# Revit family: Graypants_Chrona_Sconce10_R21_0925
name_source: partatom
category: Lighting Fixtures
units: mm (PartAtom-declared; Revit-internal decimal feet)

## family parameters
Cut with Voids When Loaded = No
Host = Face
Light Source = Yes
Part Type = Normal
Room Calculation Point = No
Round Connector Dimension = Use Diameter
Shared = No

## types (1)
- Graypants_Chrona_Sconce10 (diameter 10")
    Color Filter = 16777215
    Default Elevation = 4' - 0"
    Dimming Lamp Color Temperature Shift = <None>
    Graypants_Apparent_Load = Sconce10 - 12W
    Graypants_Cord_Material_Finish = _Graypants_Black_Finish
    Graypants_Description = Mimicking the phosphorescent envelope found around stars, Chrona lights create a luminous glow by combining spun brass and diffused acrylic. 
With a variety of configurations in both horizontal and vertical orientations, Dish pendants can be clustered together to make stunning 
constellations or individually hung to accentuate any space.
    Graypants_Dimming = 0-10v
    Graypants_Initial_Color_Temperature = 2700K
    Graypants_Initial_Intensity = Sconce10 - 615 Lumens
    Graypants_Manufacturer = Graypants
    Graypants_Material_Finish = _Graypants_Brass
    Graypants_Model = Sconce10
    Graypants_Product_Visible = Yes
    Graypants_SKU = Sconce10 Brass: GP2010-B
    Graypants_Shade_Finish_Options = Brass
    Graypants_Spec_Sheet = https://www.dropbox.com
    Graypants_URL = www.graypants.com
    Graypants_Voltage = 120-277V
    Light Source Symbol Size = 0' - 9 17/32"

## geometry (parser evidence)
native form markers: Sweep x6
no freeform markers — native parametric forms only
